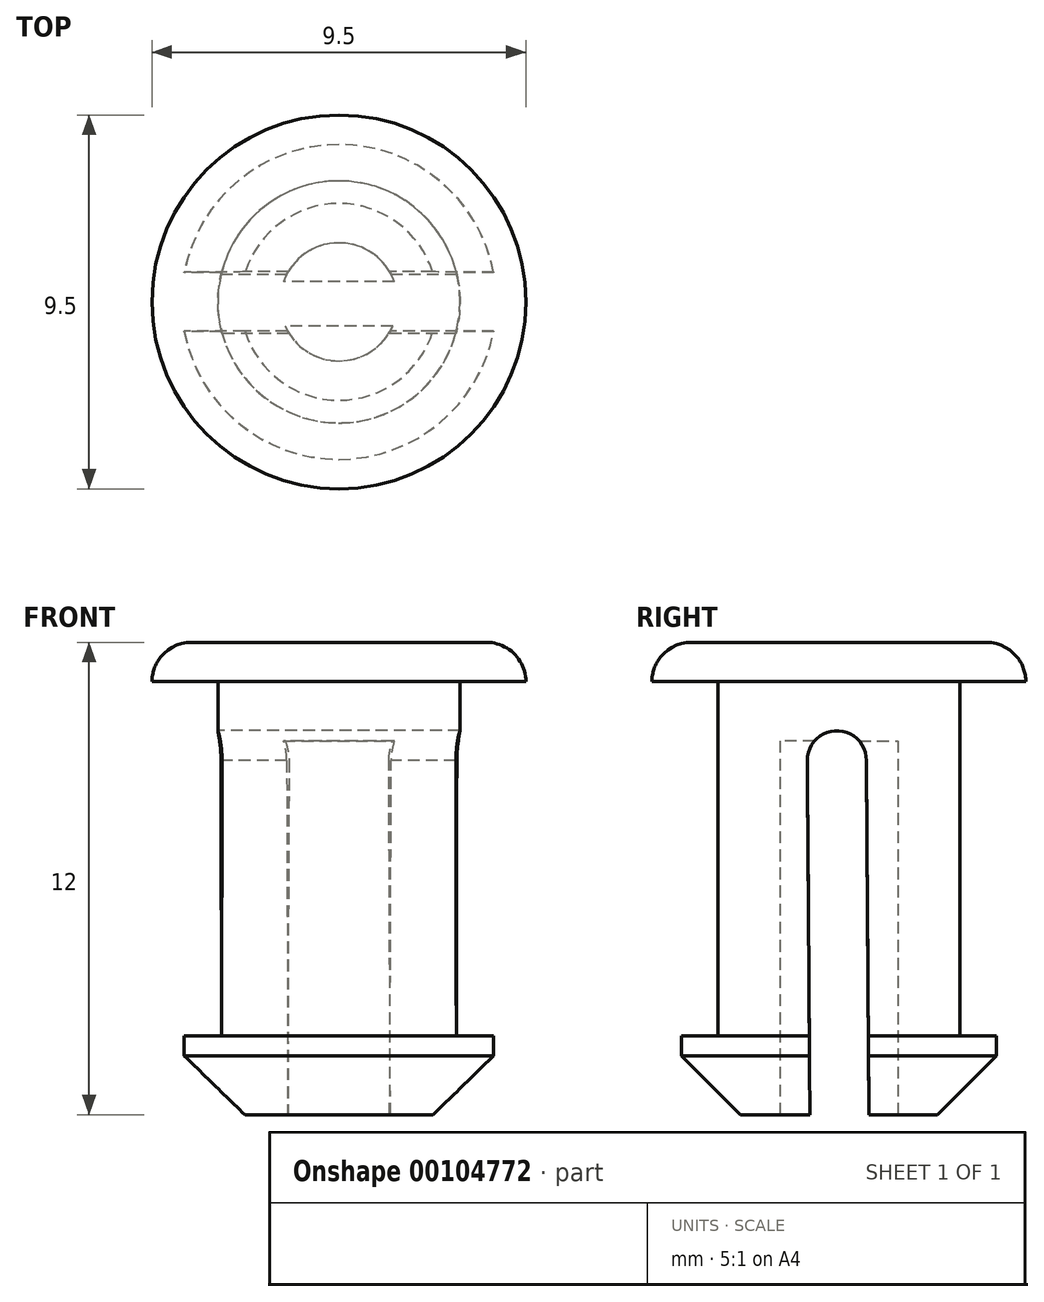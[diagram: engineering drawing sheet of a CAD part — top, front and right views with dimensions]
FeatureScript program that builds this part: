
annotation { "Feature Type Name" : "Feature", "Feature Type Description" : "" }
export const myFeature = defineFeature(function(context is Context, id is Id, definition is map)
    precondition{}
    {
        {
            var Q0;
            Q0=qCreatedBy(makeId("Top.planeOp"),FACE);
            var sketch = newSketch(context, id + "F0", { "sketchPlane" : qUnion([Q0])});
            skCircle(sketch, "E0", {"center": v(0, 0) * mm, "radius": 3.08 * mm});
            skSolve(sketch);
        }
        {
            var Q0;
            Q0=makeQuery(id+"F0.imprint","IMPRINT",FACE,{"disambiguationData":[TD([[makeQuery(id+"F0.imprint","IMPRINT",EDGE,{"derivedFrom":sQuery(id+"F0.wireOp",EDGE,"E0")}),1.0]])]});
            extrude(context, id + "F1", {"entities" : qUnion([Q0]), "depth" : 9 * mm});
        }
        {
            var Q0;
            Q0=makeQuery(id+"F1.opExtrude","CAP_FACE",FACE,{"disambiguationData":[OSD([sQuery(id+"F0.wireOp",EDGE,"E0")])],"isStart":false});
            var sketch = newSketch(context, id + "F2", { "sketchPlane" : qUnion([Q0])});
            skCircle(sketch, "E1", {"center": v(0, 0) * mm, "radius": 4.75 * mm});
            skSolve(sketch);
        }
        {
            var Q0;
            Q0=makeQuery(id+"F2.imprint","IMPRINT",FACE,{"disambiguationData":[TD([[makeQuery(id+"F2.imprint","IMPRINT",EDGE,{"derivedFrom":makeQuery(id+"F1.opExtrude","CAP_EDGE",EDGE,{"disambiguationData":[OSD([sQuery(id+"F0.wireOp",EDGE,"E0")])],"isStart":false})}),1.0]])]});
            var Q1;
            Q1=makeQuery(id+"F2.imprint","IMPRINT",FACE,{"disambiguationData":[TD([[makeQuery(id+"F2.imprint","IMPRINT",EDGE,{"derivedFrom":sQuery(id+"F2.wireOp",EDGE,"E1")}),1.0]])]});
            extrude(context, id + "F3", {"entities" : qUnion([Q0, Q1]), "operationType" : NewBodyOperationType.ADD, "depth" : 1 * mm});
        }
        {
            var Q0;
            Q0=makeQuery(id+"F3.opExtrude","CAP_EDGE",EDGE,{"disambiguationData":[OSD([sQuery(id+"F2.wireOp",EDGE,"E1")])],"isStart":false});
            fillet(context, id + "F4", {"entities" : qUnion([Q0]), "radius" : 1 * mm, "tangentPropagation" : true, "allowEdgeOverflow" : false});
        }
        {
            var Q0;
            Q0=makeQuery(id+"F1.opExtrude","CAP_FACE",FACE,{"disambiguationData":[OSD([sQuery(id+"F0.wireOp",EDGE,"E0")])],"isStart":true});
            var sketch = newSketch(context, id + "F5", { "sketchPlane" : qUnion([Q0])});
            skCircle(sketch, "E2", {"center": v(0, 0) * mm, "radius": 4 * mm});
            skSolve(sketch);
        }
        {
            var Q0;
            Q0=makeQuery(id+"F5.imprint","IMPRINT",FACE,{"disambiguationData":[TD([[makeQuery(id+"F5.imprint","IMPRINT",EDGE,{"derivedFrom":sQuery(id+"F5.wireOp",EDGE,"E2")}),1.0]])]});
            var Q1;
            Q1=makeQuery(id+"F5.imprint","IMPRINT",FACE,{"disambiguationData":[TD([[makeQuery(id+"F5.imprint","IMPRINT",EDGE,{"derivedFrom":makeQuery(id+"F1.opExtrude","CAP_EDGE",EDGE,{"disambiguationData":[OSD([sQuery(id+"F0.wireOp",EDGE,"E0")])],"isStart":true})}),-1.0]])]});
            extrude(context, id + "F6", {"entities" : qUnion([Q0, Q1]), "operationType" : NewBodyOperationType.ADD, "depth" : 2 * mm});
        }
        {
            var Q0;
            Q0=makeQuery(id+"F6.opExtrude","CAP_FACE",FACE,{"disambiguationData":[OSD([sQuery(id+"F5.wireOp",EDGE,"E2")])],"isStart":false});
            chamfer(context, id + "F7", {"entities" : qUnion([Q0]), "width" : 1.5 * mm, "tangentPropagation" : true});
        }
        {
            var Q0;
            Q0=makeQuery(id+"F6.opExtrude","CAP_FACE",FACE,{"disambiguationData":[OSD([sQuery(id+"F5.wireOp",EDGE,"E2")])],"isStart":false});
            var sketch = newSketch(context, id + "F8", { "sketchPlane" : qUnion([Q0])});
            skCircle(sketch, "E3", {"center": v(0, 0) * mm, "radius": 1.5 * mm});
            skSolve(sketch);
        }
        {
            var Q0;
            Q0=makeQuery(id+"F8.imprint","IMPRINT",FACE,{"disambiguationData":[TD([[makeQuery(id+"F8.imprint","IMPRINT",EDGE,{"derivedFrom":sQuery(id+"F8.wireOp",EDGE,"E3")}),1.0]])]});
            extrude(context, id + "F9", {"entities" : qUnion([Q0]), "operationType" : NewBodyOperationType.REMOVE, "oppositeDirection" : true, "depth" : 9.5 * mm});
        }
        {
            var Q0;
            Q0=qCreatedBy(makeId("Right.planeOp"),FACE);
            var sketch = newSketch(context, id + "F10", { "sketchPlane" : qUnion([Q0])});
            skLineSegment(sketch, "E4.bottom", {"start": v(0.8, -7) * mm, "end": v(-0.7, -7) * mm});
            skLineSegment(sketch, "E4.left", {"start": v(0.8, -7) * mm, "end": v(0.7, 7) * mm});
            skLineSegment(sketch, "E4.right", {"start": v(-0.7, -7) * mm, "end": v(-0.8, 7) * mm});
            skPoint(sketch, "E4.middle", {"position": v(0, 0) * mm});
            skArc(sketch, "E5", {"start": v(0.7, 7) * mm, "mid": v(-0.05, 7.76) * mm, "end": v(-0.8, 7) * mm});
            skSolve(sketch);
        }
        {
            var Q0;
            Q0=makeQuery(id+"F10.imprint","IMPRINT",FACE,{"disambiguationData":[TD([[makeQuery(id+"F10.imprint","IMPRINT",EDGE,{"derivedFrom":sQuery(id+"F10.wireOp",EDGE,"E4.bottom")}),-1.0]])]});
            extrude(context, id + "F11", {"entities" : qUnion([Q0]), "operationType" : NewBodyOperationType.REMOVE, "depth" : 25 * mm, "hasSecondDirection" : true, "secondDirectionOppositeDirection" : true, "secondDirectionDepth" : 25 * mm});
        }
    });
